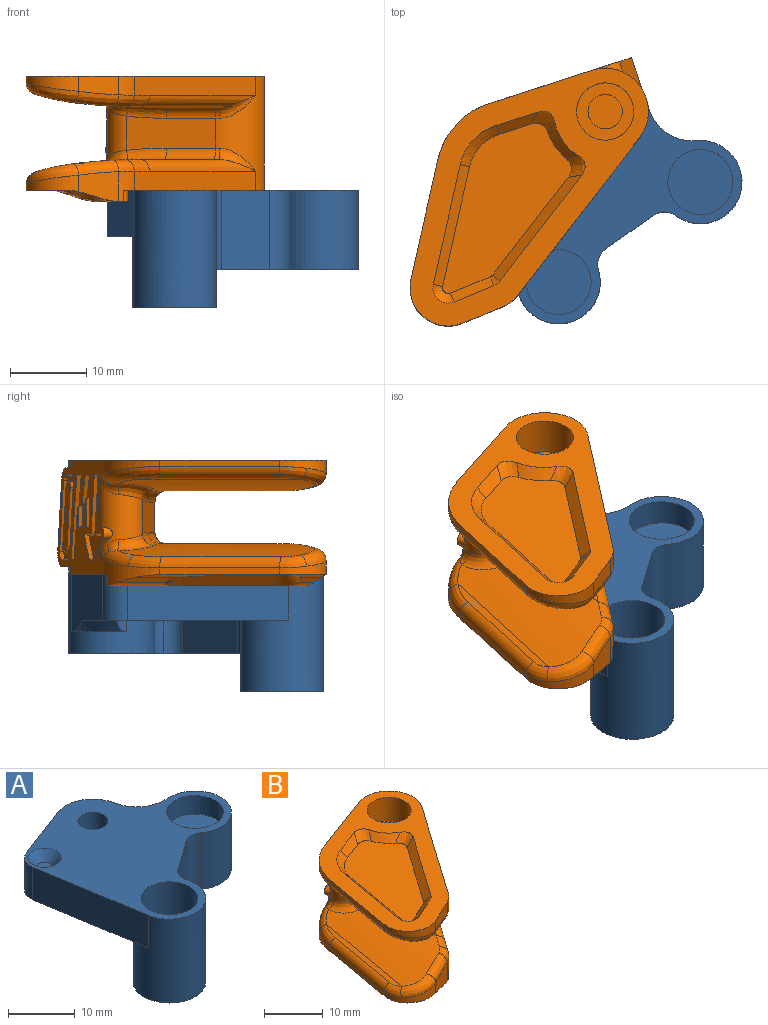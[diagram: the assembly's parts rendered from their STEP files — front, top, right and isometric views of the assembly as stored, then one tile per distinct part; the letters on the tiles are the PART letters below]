
ASSEMBLY  parts=2 mates=1
PART A: 54 faces, bbox 32.8x34.4x15.4 mm
  f0: plane 26.37x23.56mm, normal (0,0,-1), area 193mm2, adj f2,f4,f7,f11,f12,f13,f14,f15
  f1: cylinder r=2.75mm len=6.75mm, axis (0,0,-1), area 116.6mm2, adj f5,f28
  f2: cylinder r=2.75mm len=6.75mm, axis (0,0,-1), area 116.6mm2, adj f0,f27
  f3: cylinder r=2.25mm len=5.03mm, axis (0,0,-1), area 71mm2, adj f6,f26
  f4: cylinder r=5.45mm len=15.38mm, axis (0,0,-1), area 402.9mm2, adj f0,f5,f6,f10,f14,f37,f38,f48
  f5: plane 10.9x10.9mm, normal (0,0,-1), area 69.6mm2, adj f1,f4
  f6: plane 33.4x32.79mm, normal (0,0,1), area 477.1mm2, adj f3,f4,f7,f8,f9,f10,f11,f12
  f7: cylinder r=5.66mm len=11.31mm, axis (0,0,-1), area 182.4mm2, adj f0,f6,f8,f11,f35,f40,f45,f53
  f8: plane 10.96x7.5mm, normal (-0.35,0.94,0), area 74.5mm2, adj f6,f7,f9,f52,f53
  f9: cylinder r=3mm len=6mm, axis (0,0,-1), area 24.7mm2, adj f6,f8,f10,f52
  f10: plane 21.06x6mm, normal (-0.99,-0.16,0), area 128mm2, adj f4,f6,f9,f52
  f11: cylinder r=5.93mm len=10.38mm, axis (0,0,-1), area 91.1mm2, adj f0,f6,f7,f13
  f12: plane 10.38x6.21mm, normal (0.58,-0.82,0), area 78.9mm2, adj f0,f6,f14,f15
  f13: cylinder r=5.45mm len=10.9mm, axis (0,0,-1), area 218.9mm2, adj f0,f6,f11,f15
  f14: cylinder r=2.5mm len=10.38mm, axis (0,0,-1), area 32.4mm2, adj f0,f4,f6,f12
  f15: cylinder r=2.5mm len=10.38mm, axis (0,0,-1), area 32.4mm2, adj f0,f6,f12,f13
  f16: plane 8.5x8.5mm, normal (0,0,1), area 56.7mm2, adj f17
  f17: cylinder r=4.25mm len=8.5mm, axis (0,0,1), area 90.1mm2, adj f6,f16
  f18: plane 8.5x8.5mm, normal (0,0,1), area 56.7mm2, adj f19
  f19: cylinder r=4.25mm len=8.5mm, axis (0,0,1), area 223.6mm2, adj f6,f18
  f20: plane 5.35x3.77mm, normal (0.42,0.91,0), area 22.2mm2, adj f0,f21,f25,f26
  f21: plane 5.35x4.14mm, normal (1,0.09,0), area 22.2mm2, adj f0,f20,f22,f26
  f22: plane 5.35x3.4mm, normal (0.58,-0.82,0), area 22.2mm2, adj f0,f21,f23,f26
  f23: plane 5.35x3.77mm, normal (-0.42,-0.91,0), area 22.2mm2, adj f0,f22,f24,f26
  f24: plane 5.35x4.14mm, normal (-1,-0.09,0), area 22.2mm2, adj f0,f23,f25,f26
  f25: plane 5.35x3.4mm, normal (-0.58,0.82,0), area 22.2mm2, adj f0,f20,f24,f26
  f26: plane 8.28x7.55mm, normal (0,0,-1), area 29mm2, adj f3,f20,f21,f22,f23,f24,f25
  f27: plane 5.5x5.5mm, normal (0,0,-1), area 23.8mm2, adj f2
  f28: plane 5.5x5.5mm, normal (0,0,-1), area 23.8mm2, adj f1
  f29: plane 2x2mm, normal (0,0,1), area 3.1mm2, adj f30
  f30: cone r=1mm half-angle=45deg, axis (0,0,1), area 23.3mm2, adj f6,f29
  f31: plane 15.5x13.39mm, normal (0,0,-1), area 102.6mm2, adj f41,f42,f43,f44,f45,f46,f47,f48
  f32: plane 10.25x7.23mm, normal (-0.58,0.82,0), area 73.7mm2, adj f0,f36,f37,f51
  f33: plane 11.5x1.84mm, normal (0.99,0.16,0), area 17.5mm2, adj f38,f39,f44,f52
  f34: plane 2.37x1.5mm, normal (0.35,-0.94,0), area 3.8mm2, adj f39,f40,f41,f52
  f35: cylinder r=3.35mm len=5.88mm, axis (0,0,-1), area 30.9mm2, adj f0,f7,f36,f47
  f36: cylinder r=2mm len=5.88mm, axis (0,0,-1), area 16.2mm2, adj f0,f32,f35,f49
  f37: cylinder r=2mm len=5.88mm, axis (0,0,-1), area 8.5mm2, adj f0,f4,f32,f50
  f38: cylinder r=2mm len=2.41mm, axis (0,0,-1), area 4.9mm2, adj f4,f33,f46,f52
  f39: cylinder r=2mm len=2.19mm, axis (0,0,-1), area 4.1mm2, adj f33,f34,f42,f52
  f40: cylinder r=2mm len=3mm, axis (0,0,-1), area 7mm2, adj f7,f34,f43,f52,f53
  f41: plane 2.9x2.29mm, normal (0.25,-0.66,-0.71), area 5.4mm2, adj f31,f34,f42,f43
  f42: cone r=0.5mm half-angle=45deg, axis (0,0,-1), area 3.6mm2, adj f31,f39,f41,f44
  f43: cone r=0.5mm half-angle=45deg, axis (0,0,-1), area 4.2mm2, adj f31,f40,f41,f45
  f44: plane 11.73x3.33mm, normal (0.7,0.11,-0.71), area 24.7mm2, adj f31,f33,f42,f46
  f45: cone r=5.66mm half-angle=45deg, axis (0,0,1), area 22.3mm2, adj f7,f31,f43,f47
  f46: cone r=0.5mm half-angle=45deg, axis (0,0,-1), area 4.3mm2, adj f31,f38,f44,f48
  f47: cone r=1.85mm half-angle=45deg, axis (0,0,-1), area 8.7mm2, adj f31,f35,f45,f49
  f48: cone r=6.95mm half-angle=45deg, axis (0,0,1), area 4.3mm2, adj f4,f31,f46,f50
  f49: cone r=0.5mm half-angle=45deg, axis (0,0,-1), area 3.7mm2, adj f31,f36,f47,f51
  f50: cone r=0.5mm half-angle=45deg, axis (0,0,-1), area 1.9mm2, adj f31,f37,f48,f51
  f51: plane 11.11x8.46mm, normal (-0.41,0.58,-0.71), area 26.6mm2, adj f31,f32,f49,f50
  f52: plane 26.91x8.8mm, normal (0,0,-1), area 82.5mm2, adj f4,f8,f9,f10,f33,f34,f38,f39
  f53: cone r=5.66mm half-angle=45deg, axis (0,0,1), area 12.1mm2, adj f7,f8,f40,f52
PART B: 153 faces, bbox 33.9x47x18.4 mm
  f0: plane 18.36x14.91mm, normal (-0.35,0.94,0), area 133.2mm2, adj f1,f3,f4,f6,f12,f16,f34,f42
  f1: cylinder r=3mm len=10.75mm, axis (0,0,-1), area 45.1mm2, adj f0,f13,f30,f31,f32,f56,f57,f58
  f2: plane 18.36x5.22mm, normal (0,0,-1), area 43.4mm2, adj f7,f8,f73,f78,f97,f98
  f3: plane 32.98x23.65mm, normal (0,0,-1), area 218.4mm2, adj f0,f6,f10,f11,f12,f61,f63,f80
  f4: plane 35.78x31.22mm, normal (0,0,1), area 287.1mm2, adj f0,f12,f34,f35,f36,f37,f38,f39
  f5: plane 14.4x9.67mm, normal (0,0,1), area 52mm2, adj f15,f25,f27,f28
  f6: cylinder r=10mm len=7.63mm, axis (0,0,-1), area 18.7mm2, adj f0,f3,f7,f17,f18,f95,f96,f98
  f7: plane 15.83x2.8mm, normal (-0.98,0.17,0), area 13.4mm2, adj f2,f6,f8,f19,f98
  f8: cylinder r=5mm len=7.11mm, axis (0,0,-1), area 14.6mm2, adj f2,f7,f9,f20,f21,f97
  f9: plane 5.11x3.92mm, normal (0.42,-0.91,0), area 17.8mm2, adj f8,f10,f22,f94,f96,f97
  f10: cylinder r=5mm len=3.98mm, axis (0,0,-1), area 7.6mm2, adj f3,f9,f11,f23,f89,f96,f100
  f11: plane 21.24x14.87mm, normal (0.82,-0.57,0), area 64.8mm2, adj f3,f10,f12,f24,f25
  f12: cylinder r=5.66mm len=14.91mm, axis (0,0,-1), area 179.6mm2, adj f0,f3,f4,f11,f13,f26,f27,f39
  f13: plane 11.66x4.44mm, normal (-0.09,-1,0), area 46.7mm2, adj f1,f12,f28,f29,f54,f55
  f14: plane 21.86x4.38mm, normal (-0.24,0.04,0.97), area 18.6mm2, adj f15,f18,f19,f20
  f15: cylinder r=50mm len=27.28mm, axis (0.17,0.98,0), area 254.8mm2, adj f5,f14,f17,f21,f22,f23,f24,f29
  f16: bspline ~11.99x5.56mm, area 1.5mm2, adj f0,f17,f32
  f17: bspline ~6.87x6.17mm, area 11mm2, adj f6,f15,f16,f18,f31
  f18: bspline ~5.22x3.22mm, area 8.7mm2, adj f6,f14,f17,f19
  f19: cylinder r=1.5mm len=16.02mm, axis (-0.17,-0.98,0), area 32mm2, adj f7,f14,f18,f20
  f20: bspline ~3.51x1.68mm, area 6.5mm2, adj f8,f14,f19,f21
  f21: bspline ~7.15x3.92mm, area 15.2mm2, adj f8,f15,f20,f22
  f22: bspline ~19.62x10.15mm, area 14mm2, adj f9,f15,f21,f23
  f23: bspline ~4x3.6mm, area 5.6mm2, adj f10,f15,f22,f24
  f24: bspline ~21.39x15.82mm, area 7.7mm2, adj f11,f15,f23,f25
  f25: cylinder r=1.5mm len=19.44mm, axis (-0.57,-0.82,0), area 46.6mm2, adj f5,f11,f24,f26
  f26: bspline ~4.58x3.91mm, area 4.5mm2, adj f12,f25,f27
  f27: torus R=7.16mm, axis (0,0,1), area 1.4mm2, adj f5,f12,f26,f28
  f28: cylinder r=1.5mm len=6.58mm, axis (-1,0.09,0), area 15.2mm2, adj f5,f13,f27,f29
  f29: bspline ~5.21x1.95mm, area 12.2mm2, adj f13,f15,f28,f30
  f30: bspline ~4.95x4.87mm, area 11.9mm2, adj f1,f15,f29,f31
  f31: bspline ~2.16x1.93mm, area 2.6mm2, adj f1,f17,f30,f32
  f32: bspline ~2.46x1.99mm, area 1.2mm2, adj f1,f16,f31
  f33: plane 14.4x9.67mm, normal (0,0,-1), area 52mm2, adj f41,f51,f53,f54
  f34: cylinder r=10mm len=7.63mm, axis (0,0,1), area 12.4mm2, adj f0,f4,f35,f43,f44
  f35: plane 15.82x2.79mm, normal (-0.98,0.17,0), area 13.3mm2, adj f4,f34,f36,f45
  f36: cylinder r=5mm len=7.11mm, axis (0,0,1), area 14.4mm2, adj f4,f35,f37,f46,f47
  f37: plane 5.1x2.43mm, normal (0.42,-0.91,0), area 12.6mm2, adj f4,f36,f38,f48
  f38: cylinder r=5mm len=2.48mm, axis (0,0,1), area 6.4mm2, adj f4,f37,f39,f49
  f39: plane 21.24x14.87mm, normal (0.82,-0.57,0), area 64.8mm2, adj f4,f12,f38,f50,f51
  f40: plane 21.86x4.38mm, normal (-0.24,0.04,-0.97), area 18.6mm2, adj f41,f44,f45,f46
  f41: cylinder r=50mm len=27.28mm, axis (0.17,0.98,0), area 254.8mm2, adj f33,f40,f43,f47,f48,f49,f50,f55
  f42: bspline ~11.99x5.56mm, area 1.5mm2, adj f0,f43,f58
  f43: bspline ~7.83x6.4mm, area 11mm2, adj f34,f41,f42,f44,f57
  f44: bspline ~5.22x3.22mm, area 8.7mm2, adj f34,f40,f43,f45
  f45: cylinder r=1.5mm len=16.02mm, axis (-0.17,-0.98,0), area 32mm2, adj f35,f40,f44,f46
  f46: bspline ~3.51x1.68mm, area 6.5mm2, adj f36,f40,f45,f47
  f47: bspline ~7.85x3.92mm, area 15.2mm2, adj f36,f41,f46,f48
  f48: bspline ~19.62x10.15mm, area 14mm2, adj f37,f41,f47,f49
  f49: bspline ~4x3.6mm, area 5.6mm2, adj f38,f41,f48,f50
  f50: bspline ~21.39x15.82mm, area 7.7mm2, adj f39,f41,f49,f51
  f51: cylinder r=1.5mm len=19.44mm, axis (-0.57,-0.82,0), area 46.6mm2, adj f33,f39,f50,f52
  f52: bspline ~5.17x4.06mm, area 4.6mm2, adj f12,f51,f53
  f53: torus R=7.16mm, axis (0,0,-1), area 1.4mm2, adj f12,f33,f52,f54
  f54: cylinder r=1.5mm len=6.58mm, axis (-1,0.09,0), area 15.2mm2, adj f13,f33,f53,f55
  f55: bspline ~5.21x1.95mm, area 12.2mm2, adj f13,f41,f54,f56
  f56: bspline ~4.95x4.87mm, area 11.9mm2, adj f1,f41,f55,f57
  f57: bspline ~2.16x1.93mm, area 2.6mm2, adj f1,f43,f56,f58
  f58: bspline ~2.46x1.99mm, area 1.2mm2, adj f1,f42,f57
  f59: plane 7.5x7.5mm, normal (0,0,1), area 28.3mm2, adj f60,f61
  f60: cylinder r=3.75mm len=7.5mm, axis (0,0,1), area 116.3mm2, adj f4,f59
  f61: cylinder r=2.25mm len=9.98mm, axis (0,0,1), area 141mm2, adj f3,f59
  f62: plane 2x2mm, normal (0,0,-1), area 3.1mm2, adj f63
  f63: cone r=1mm half-angle=45deg, axis (0,0,1), area 13.3mm2, adj f3,f62
  f64: cone r=6.75mm half-angle=45deg, axis (0,0,-1), area 8.7mm2, adj f4,f72,f92,f93
  f65: plane 5.32x3.17mm, normal (0.25,-0.66,0.71), area 8.9mm2, adj f4,f66,f72,f92
  f66: cone r=7mm half-angle=45deg, axis (0,0,1), area 11.7mm2, adj f4,f65,f67,f72
  f67: plane 16.04x4.02mm, normal (0.7,-0.12,0.71), area 28.4mm2, adj f4,f66,f68,f72
  f68: cone r=2mm half-angle=45deg, axis (0,0,1), area 5.3mm2, adj f4,f67,f69,f72
  f69: plane 5.63x3.51mm, normal (-0.3,0.64,0.71), area 10mm2, adj f4,f68,f70,f72
  f70: cone r=2mm half-angle=45deg, axis (0,0,1), area 1.3mm2, adj f4,f69,f71,f72
  f71: plane 14.31x11.04mm, normal (-0.58,0.41,0.71), area 29.7mm2, adj f4,f70,f72,f93
  f72: plane 23.68x17.02mm, normal (0,0,1), area 201mm2, adj f64,f65,f66,f67,f68,f69,f70,f71
  f73: plane 13.73x3.6mm, normal (0.7,-0.12,-0.71), area 26mm2, adj f2,f74,f78,f79,f98
  f74: cone r=1.5mm half-angle=45deg, axis (0,0,-1), area 13mm2, adj f73,f75,f79,f95,f96,f98
  f75: plane 12.35x4.62mm, normal (-0.7,-0.11,-0.71), area 46.8mm2, adj f74,f76,f79,f96
  f76: cone r=2mm half-angle=45deg, axis (0,0,-1), area 9.9mm2, adj f75,f77,f79,f94,f96
  f77: plane 4.34x2.81mm, normal (-0.3,0.64,-0.71), area 8.9mm2, adj f76,f78,f79,f94,f97
  f78: cone r=2mm half-angle=45deg, axis (0,0,-1), area 5.4mm2, adj f2,f73,f77,f79,f97
  f79: plane 14.53x4.8mm, normal (0,0,-1), area 37.5mm2, adj f73,f74,f75,f76,f77,f78
  f80: cone r=5.25mm half-angle=45deg, axis (0,0,1), area 6.4mm2, adj f3,f85,f90,f91
  f81: plane 8.38x6.89mm, normal (-0.58,0.41,-0.71), area 16.9mm2, adj f3,f82,f85,f91
  f82: cone r=2mm half-angle=45deg, axis (0,0,-1), area 5.8mm2, adj f3,f81,f83,f85
  f83: plane 4.76x1.97mm, normal (0.7,0.11,-0.71), area 8.2mm2, adj f3,f82,f84,f85
  f84: cone r=9.98mm half-angle=45deg, axis (0,0,-1), area 16.9mm2, adj f3,f83,f85,f90
  f85: plane 14.79x9.26mm, normal (0,0,-1), area 61.9mm2, adj f80,f81,f82,f83,f84,f90,f91
  f86: cylinder r=3.1mm len=1.5mm, axis (0,0,1), area 1.3mm2, adj f3,f87,f89,f99
  f87: plane 21.06x3.38mm, normal (0.99,0.16,0), area 32mm2, adj f3,f86,f88,f89
  f88: cylinder r=5.55mm len=1.5mm, axis (0,0,1), area 2.1mm2, adj f3,f87,f89,f100
  f89: plane 25.75x4.72mm, normal (0,0,-1), area 14.1mm2, adj f10,f86,f87,f88,f96,f99,f100
  f90: bspline ~3.89x3.71mm, area 7.6mm2, adj f3,f80,f84,f85
  f91: bspline ~4.08x3.32mm, area 5.6mm2, adj f3,f80,f81,f85
  f92: bspline ~4.19x3.91mm, area 5.6mm2, adj f4,f64,f65,f72
  f93: bspline ~3.83x3.26mm, area 5.6mm2, adj f4,f64,f71,f72
  f94: plane 2.94x2.49mm, normal (-0.28,-0.05,-0.96), area 5.3mm2, adj f9,f76,f77,f96,f97
  f95: plane 8.47x3.14mm, normal (-0.28,-0.05,-0.96), area 13.5mm2, adj f6,f74,f96,f98
  f96: cylinder r=10mm len=27.05mm, axis (-0.16,0.99,0), area 34.3mm2, adj f6,f9,f10,f74,f75,f76,f89,f94
  f97: cylinder r=10mm len=3.52mm, axis (-0.16,0.99,0), area 8.4mm2, adj f2,f8,f9,f77,f78,f94
  f98: cylinder r=10mm len=15.74mm, axis (-0.16,0.99,0), area 24.1mm2, adj f2,f6,f7,f73,f74,f95
  f99: cylinder r=1mm len=1.5mm, axis (0,0,-1), area 3.3mm2, adj f3,f6,f86,f89,f96
  f100: cylinder r=1mm len=1.5mm, axis (0,0,-1), area 2.1mm2, adj f3,f10,f88,f89
  f101: cylinder r=1.8mm len=4.43mm, axis (-0.35,0.94,0), area 8.5mm2, adj f0,f12,f102,f105
  f102: plane 9.31x3.8mm, normal (0.92,0.35,0.17), area 23.5mm2, adj f0,f12,f101,f103
  f103: cylinder r=1.8mm len=2.17mm, axis (-0.35,0.94,0), area 2.3mm2, adj f0,f12,f102,f104
  f104: plane 2.01x0.71mm, normal (0,0,1), area 0.2mm2, adj f0,f12,f103
  f105: plane 3.89x1.28mm, normal (0,0,-1), area 1.5mm2, adj f0,f12,f101
  f106: cylinder r=0.8mm len=1.43mm, axis (-0.35,0.94,0), area 1.9mm2, adj f0,f1,f107,f108
  f107: plane 2.3x2.23mm, normal (-0.65,-0.24,-0.72), area 0.9mm2, adj f0,f1,f106
  f108: plane 1.52x1.02mm, normal (0,0,1), area 0.2mm2, adj f0,f1,f106
  f109: plane 3.67x3.5mm, normal (0.39,0.68,0.62), area 2.7mm2, adj f0,f110,f116,f117
  f110: plane 3.31x1.27mm, normal (-0.18,0.47,-0.87), area 1.6mm2, adj f0,f109,f111,f117
  f111: plane 8.1x1.79mm, normal (0.62,0.77,0.15), area 4.6mm2, adj f0,f110,f112,f117
  f112: plane 1.52x0.92mm, normal (-0.18,0.47,-0.87), area 0.8mm2, adj f0,f111,f113,f117
  f113: plane 8.1x1.34mm, normal (-0.97,0.17,-0.15), area 4.6mm2, adj f0,f112,f114,f117
  f114: plane 2.86x1.61mm, normal (-0.18,0.47,-0.87), area 1.6mm2, adj f0,f113,f115,f117
  f115: plane 3.5x2.23mm, normal (-0.85,0.22,0.49), area 2.2mm2, adj f0,f114,f116,f117
  f116: plane 1.55x1mm, normal (-0.18,0.47,0.87), area 0.9mm2, adj f0,f109,f115,f117
  f117: plane 10.73x5.96mm, normal (-0.35,0.94,0), area 19.4mm2, adj f109,f110,f111,f112,f113,f114,f115,f116
  f118: plane 1.12x0.79mm, normal (-0.18,0.47,0.87), area 0.5mm2, adj f0,f119,f133,f134
  f119: plane 7.01x0.61mm, normal (0.63,0.77,0.02), area 3.9mm2, adj f0,f118,f120,f134
  f120: plane 1.71x1.01mm, normal (-0.18,0.47,-0.87), area 0.9mm2, adj f0,f119,f121,f134
  f121: plane 3.96x1.22mm, normal (-0.94,0.18,-0.29), area 2.2mm2, adj f0,f120,f122,f134
  f122: plane 0.85x0.68mm, normal (-0.18,0.47,-0.87), area 0.4mm2, adj f0,f121,f123,f134
  f123: plane 3.96x0.63mm, normal (0.63,0.77,0.04), area 2.1mm2, adj f0,f122,f124,f134
  f124: plane 1.93x1.09mm, normal (-0.18,0.47,-0.87), area 1mm2, adj f0,f123,f125,f134
  f125: plane 11.31x2.37mm, normal (-0.97,0.17,-0.19), area 6.5mm2, adj f0,f124,f126,f134
  f126: plane 1.15x0.82mm, normal (-0.18,0.47,0.87), area 0.5mm2, adj f0,f125,f127,f134
  f127: plane 7.24x1.83mm, normal (0.62,0.77,0.19), area 4.1mm2, adj f0,f126,f128,f134
  f128: plane 0.88x0.72mm, normal (-0.18,0.47,0.87), area 0.4mm2, adj f0,f127,f129,f134
  f129: plane 2.94x0.62mm, normal (-0.99,0.16,-0.04), area 1.5mm2, adj f0,f128,f130,f134
  f130: plane 1.73x1.05mm, normal (-0.18,0.47,0.87), area 0.9mm2, adj f0,f129,f131,f134
  f131: plane 4.06x1.6mm, normal (0.59,0.76,0.29), area 2.3mm2, adj f0,f130,f132,f134
  f132: plane 0.84x0.71mm, normal (-0.18,0.47,0.87), area 0.4mm2, adj f0,f131,f133,f134
  f133: plane 4.06x0.61mm, normal (-0.99,0.16,-0.02), area 2.2mm2, adj f0,f118,f132,f134
  f134: plane 10.73x6.76mm, normal (-0.35,0.94,0), area 23.9mm2, adj f118,f119,f120,f121,f122,f123,f124,f125
  f135: cone r=0.5mm half-angle=30deg, axis (0.35,-0.94,0), area 0.5mm2, adj f136,f150,f151,f152
  f136: plane 0.92x0.75mm, normal (-0.18,0.47,-0.87), area 0.5mm2, adj f135,f137,f151,f152
  f137: cone r=0.5mm half-angle=30deg, axis (0.35,-0.94,0), area 0.6mm2, adj f136,f138,f151,f152
  f138: plane 7.96x1.75mm, normal (0.62,0.77,0.15), area 4.6mm2, adj f137,f139,f151,f152
  f139: cone r=0.5mm half-angle=30deg, axis (0.35,-0.94,0), area 0.5mm2, adj f138,f140,f151,f152
  f140: plane 0.92x0.75mm, normal (-0.18,0.47,0.87), area 0.5mm2, adj f139,f141,f151,f152
  f141: cone r=0.5mm half-angle=30deg, axis (0.35,-0.94,0), area 0.6mm2, adj f140,f150,f151,f152
  f142: cone r=1mm half-angle=30deg, axis (-0.35,0.94,0), area 0.9mm2, adj f0,f143,f149,f151
  f143: plane 2.25x1.25mm, normal (-0.18,0.47,-0.87), area 1.3mm2, adj f0,f142,f144,f151
  f144: cone r=1mm half-angle=30deg, axis (-0.35,0.94,0), area 0.7mm2, adj f0,f143,f145,f151
  f145: plane 9.36x1.63mm, normal (-0.97,0.17,-0.15), area 5.5mm2, adj f0,f144,f146,f151
  f146: cone r=1mm half-angle=30deg, axis (-0.35,0.94,0), area 0.9mm2, adj f0,f145,f147,f151
  f147: plane 2.25x1.25mm, normal (-0.18,0.47,0.87), area 1.3mm2, adj f0,f146,f148,f151
  f148: cone r=1mm half-angle=30deg, axis (-0.35,0.94,0), area 0.7mm2, adj f0,f147,f149,f151
  f149: plane 9.36x1.98mm, normal (0.62,0.77,0.15), area 5.5mm2, adj f0,f142,f148,f151
  f150: plane 7.96x1.4mm, normal (-0.97,0.17,-0.15), area 4.6mm2, adj f135,f141,f151,f152
  f151: plane 10.73x4.95mm, normal (-0.35,0.94,0), area 16.7mm2, adj f135,f136,f137,f138,f139,f140,f141,f142
  f152: plane 8.91x2.99mm, normal (-0.35,0.94,0), area 15.9mm2, adj f135,f136,f137,f138,f139,f140,f141,f150
PLACE A t=(20.67,-49.91,0)mm
PLACE B rot(axis=(0,0,-1),2.7deg) t=(17.3,-50.51,0)mm
MATE revolute B.f12 <-> A.f3  axis (0,0,1) through (6.09,22.3,15.38)mm
